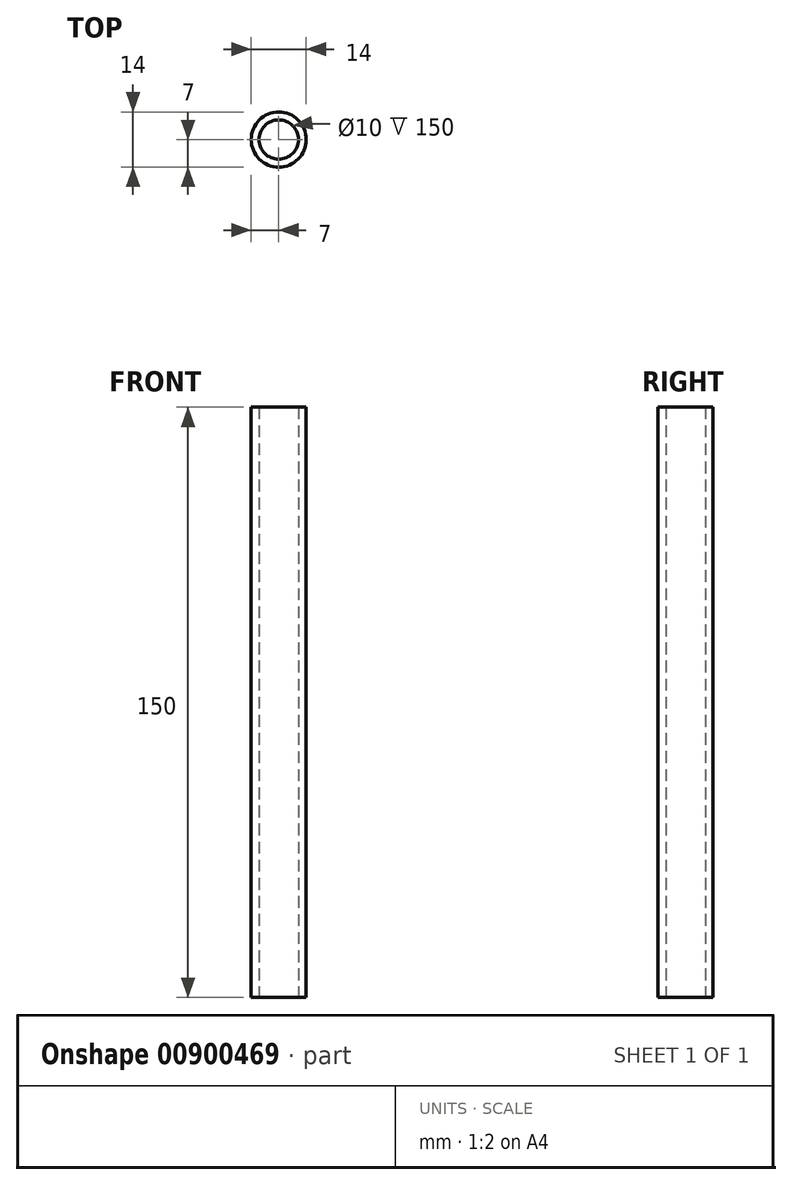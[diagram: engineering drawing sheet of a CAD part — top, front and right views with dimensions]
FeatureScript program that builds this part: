
annotation { "Feature Type Name" : "Feature", "Feature Type Description" : "" }
export const myFeature = defineFeature(function(context is Context, id is Id, definition is map)
    precondition{}
    {
        {
            var Q0;
            Q0=qCreatedBy(makeId("Top.planeOp"),FACE);
            var sketch = newSketch(context, id + "F0", { "sketchPlane" : qUnion([Q0])});
            skCircle(sketch, "E0", {"center": v(0, 0) * mm, "radius": 5 * mm});
            skCircle(sketch, "E1", {"center": v(0, 0) * mm, "radius": 7 * mm});
            skSolve(sketch);
        }
        {
            var Q0;
            Q0=makeQuery(id+"F0.imprint","IMPRINT",FACE,{"disambiguationData":[TD([[makeQuery(id+"F0.imprint","IMPRINT",EDGE,{"derivedFrom":sQuery(id+"F0.wireOp",EDGE,"E0")}),-1.0]])]});
            extrude(context, id + "F1", {"entities" : qUnion([Q0]), "depth" : 150 * mm, "offsetDistance" : 25 * mm});
        }
    });
